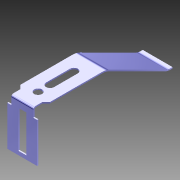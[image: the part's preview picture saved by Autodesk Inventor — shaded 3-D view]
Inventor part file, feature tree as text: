
AUTODESK INVENTOR PART (.ipt)
format: ipt  version: 2011 (Build 150239000, 239)  size: 192,512 bytes
history: native  units: mm (DEFAULTED — no unit token found)
features: other x7, sketch x6, sheet_metal_op x5, mirror x1
ambient origin geometry x8: Origin, YZ Plane, XZ Plane, XY Plane, X Axis, Y Axis, Z Axis, Center Point
bodies: Solid1 (feature_tree)
feature tree (19):
  sheet_metal_op  "Face1"
  sheet_metal_op  "Flange1"
  mirror  "Mirror1"
  other  "Corner Chamfer3"
  sheet_metal_op  "Contour Flange1"
  sketch  "Sketch2"  dims[d0=11.8872mm]
  other  "Plate1"
  sketch  "Sketch3"  dims[d1=28.575mm]
  other  "Plate2"
  sheet_metal_op  "Bend1"
  sketch  "Sketch4"  dims[d2=0.508mm]
  sketch  "Sketch5"  dims[d3=0.508mm]
  sketch  "Sketch6"  dims[d4=0.254mm]
  sketch  "Sketch8"  dims[d5=1.016mm d6=0.508mm d7=19.05mm d8=90.0deg d9=0.508mm d10=1.524mm d11=6.35mm d12=0.508mm d13=0.0mm d20=3.175mm d21=1.524mm d22=3.175mm d23=0.508mm d24=0.0mm d25=6.35mm d26=3.175mm d28=12.7mm d29=4.7752mm d30=0.508mm d31=0.0mm d32=1.524mm d33=6.35mm d43=0.508mm d44=0.254mm d45=1.016mm d46=0.508mm d47=6.35mm d48=0.508mm d49=25.4mm d50=4.7752mm d51=6.108652mm d52=45.0deg]
  other  "Plate4"
  sheet_metal_op  "Bend3"
  other  "Cut1"
  other  "Cut2"
  other  "Cut3"
